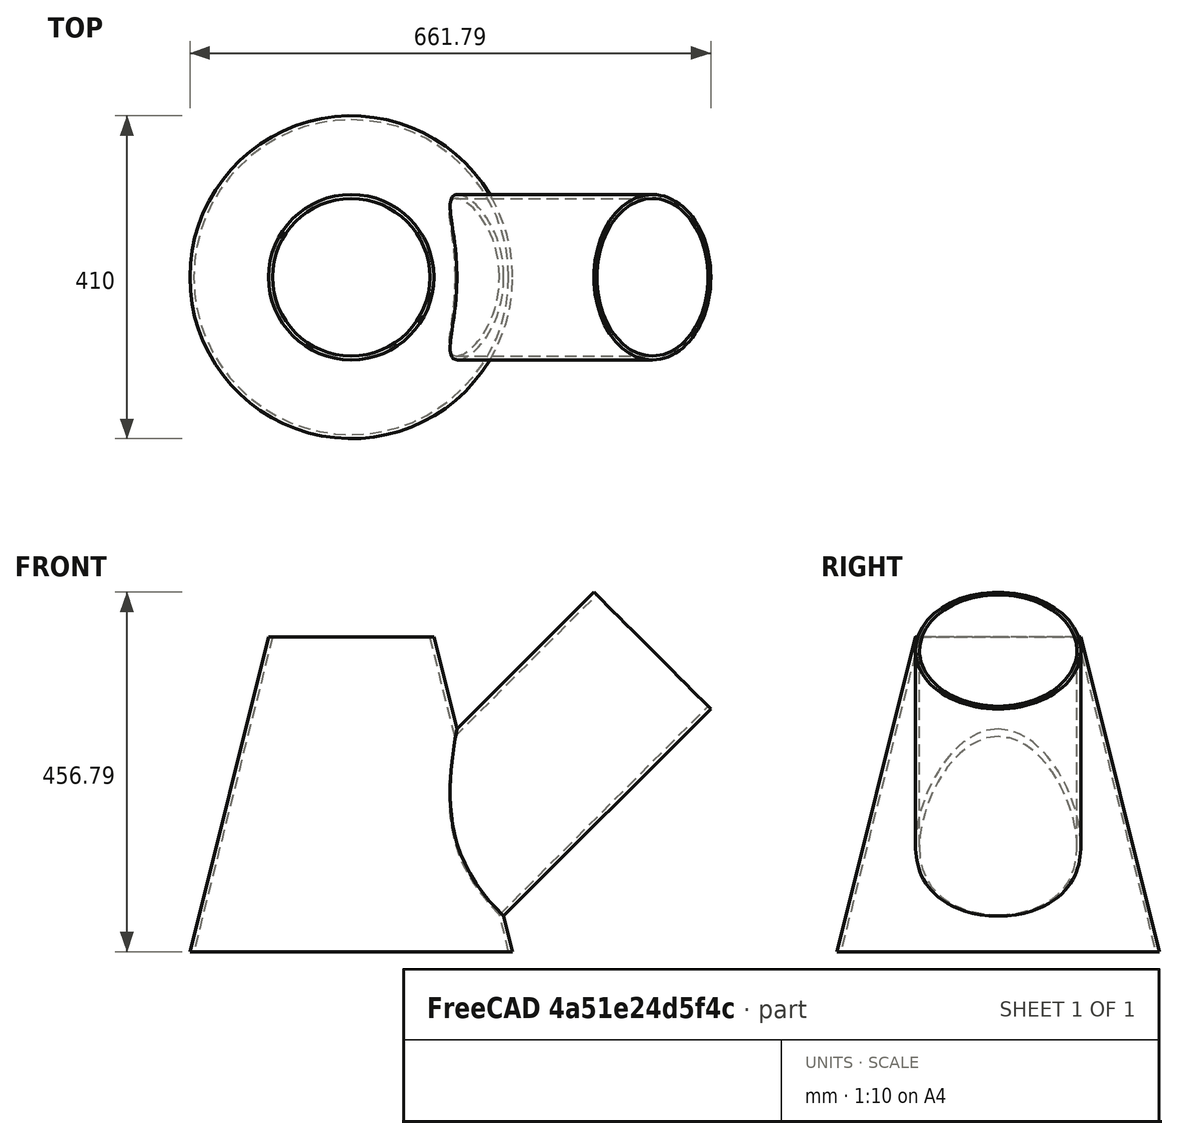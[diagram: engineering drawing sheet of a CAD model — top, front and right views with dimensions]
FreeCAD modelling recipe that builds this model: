
FCSTD DOCUMENT  (FreeCAD 0.17R13247 (Git))
Label: JUNÇÃO
License: All rights reserved
LicenseURL: http://en.wikipedia.org/wiki/All_rights_reserved
objects: Part::Cone×2, Part::Cylinder×2, Part::MultiFuse×2, Part::Cut×1
note: 7 computed .brp shape members not serialized (recipe doc carries the construction recipe); baked Part::Feature solids carry a one-line shape summary decoded from their .brp

FEATURE [Part::Cone] Cone
  Angle = 360
  AttacherType = Attacher::AttachEngine3D
  Height = 400
  Radius1 = 200
  Radius2 = 100
FEATURE [Part::Cylinder] Cylinder
  Angle = 360
  AttacherType = Attacher::AttachEngine3D
  Height = 400
  Placement = pos=(99.7021,0,99.7021) rot=(0,1,0;0.785398rad)
  Radius = 100
FEATURE [Part::MultiFuse] Fusion
  Shapes = -> [Cone,Cylinder]
FEATURE [Part::Cone] Cone001
  Angle = 360
  AttacherType = Attacher::AttachEngine3D
  Height = 400
  Radius1 = 205
  Radius2 = 105
FEATURE [Part::Cylinder] Cylinder001
  Angle = 360
  AttacherType = Attacher::AttachEngine3D
  Height = 400
  Placement = pos=(99.7021,0,99.7021) rot=(0,1,0;0.785398rad)
  Radius = 105
FEATURE [Part::MultiFuse] Fusion001
  Shapes = -> [Cone001,Cylinder001]
FEATURE [Part::Cut] Cut
  Base = -> Fusion001
  Tool = -> Fusion
